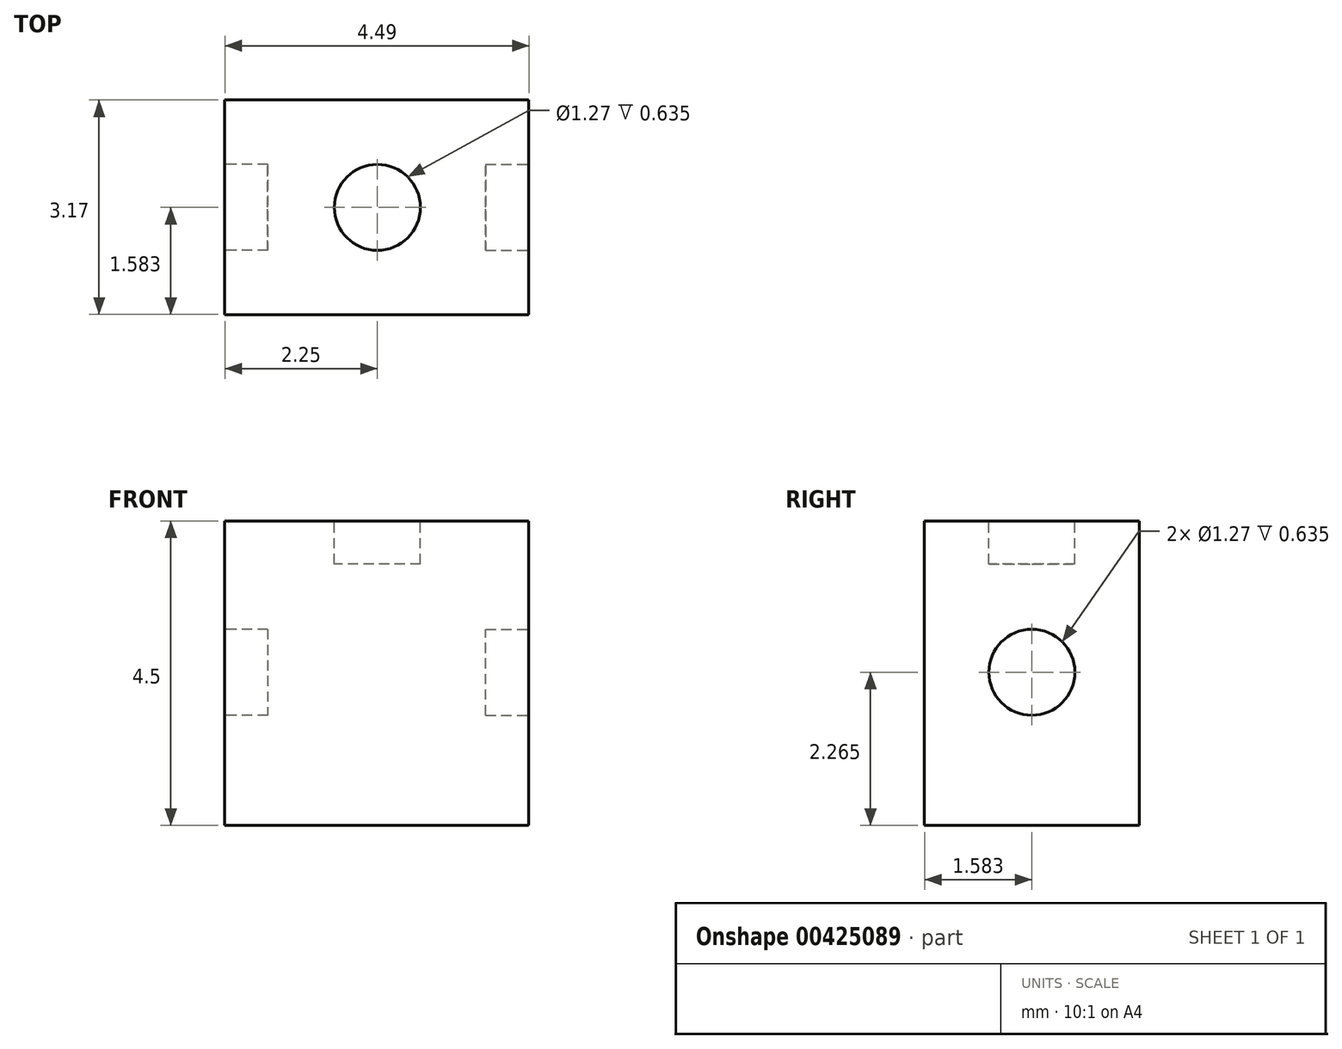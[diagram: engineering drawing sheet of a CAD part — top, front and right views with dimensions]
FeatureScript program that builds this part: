
annotation { "Feature Type Name" : "Feature", "Feature Type Description" : "" }
export const myFeature = defineFeature(function(context is Context, id is Id, definition is map)
    precondition{}
    {
        {
            var Q0;
            Q0=qCreatedBy(makeId("Front.planeOp"),FACE);
            var sketch = newSketch(context, id + "F0", { "sketchPlane" : qUnion([Q0])});
            skLineSegment(sketch, "E0.bottom", {"start": v(-14.45, 11.83) * mm, "end": v(-9.96, 11.83) * mm});
            skLineSegment(sketch, "E0.top", {"start": v(-14.45, 16.33) * mm, "end": v(-9.96, 16.33) * mm});
            skLineSegment(sketch, "E0.left", {"start": v(-14.45, 11.83) * mm, "end": v(-14.45, 16.33) * mm});
            skLineSegment(sketch, "E0.right", {"start": v(-9.96, 11.83) * mm, "end": v(-9.96, 16.33) * mm});
            skSolve(sketch);
        }
        {
            var Q0;
            Q0 = qSketchRegion(id + "F0", true);
            extrude(context, id + "F1", {"entities" : qUnion([Q0]), "depth" : 3.17 * mm});
        }
        {
            var Q0;
            Q0=makeQuery(id+"F1.opExtrude","SWEPT_FACE",FACE,{"disambiguationData":[OSD([sQuery(id+"F0.wireOp",EDGE,"E0.right")])]});
            var sketch = newSketch(context, id + "F2", { "sketchPlane" : qUnion([Q0])});
            skCircle(sketch, "E1", {"center": v(-1.59, 14.1) * mm, "radius": 0.64 * mm});
            skSolve(sketch);
        }
        {
            var Q0;
            Q0 = qSketchRegion(id + "F2", true);
            extrude(context, id + "F3", {"entities" : qUnion([Q0]), "operationType" : NewBodyOperationType.REMOVE, "oppositeDirection" : true, "depth" : 0.63 * mm});
        }
        {
            var Q0;
            Q0=makeQuery(id+"F1.opExtrude","SWEPT_FACE",FACE,{"disambiguationData":[OSD([sQuery(id+"F0.wireOp",EDGE,"E0.left")])]});
            var sketch = newSketch(context, id + "F4", { "sketchPlane" : qUnion([Q0])});
            skCircle(sketch, "E2", {"center": v(1.59, 14.1) * mm, "radius": 0.64 * mm});
            skSolve(sketch);
        }
        {
            var Q0;
            Q0 = qSketchRegion(id + "F4", true);
            extrude(context, id + "F5", {"entities" : qUnion([Q0]), "operationType" : NewBodyOperationType.REMOVE, "oppositeDirection" : true, "depth" : 0.64 * mm});
        }
        {
            var Q0;
            Q0=makeQuery(id+"F1.opExtrude","SWEPT_FACE",FACE,{"disambiguationData":[OSD([sQuery(id+"F0.wireOp",EDGE,"E0.top")])]});
            var sketch = newSketch(context, id + "F6", { "sketchPlane" : qUnion([Q0])});
            skCircle(sketch, "E3", {"center": v(-12.2, -1.59) * mm, "radius": 0.64 * mm});
            skSolve(sketch);
        }
        {
            var Q0;
            Q0 = qSketchRegion(id + "F6", true);
            extrude(context, id + "F7", {"entities" : qUnion([Q0]), "operationType" : NewBodyOperationType.REMOVE, "oppositeDirection" : true, "depth" : 0.64 * mm});
        }
    });
